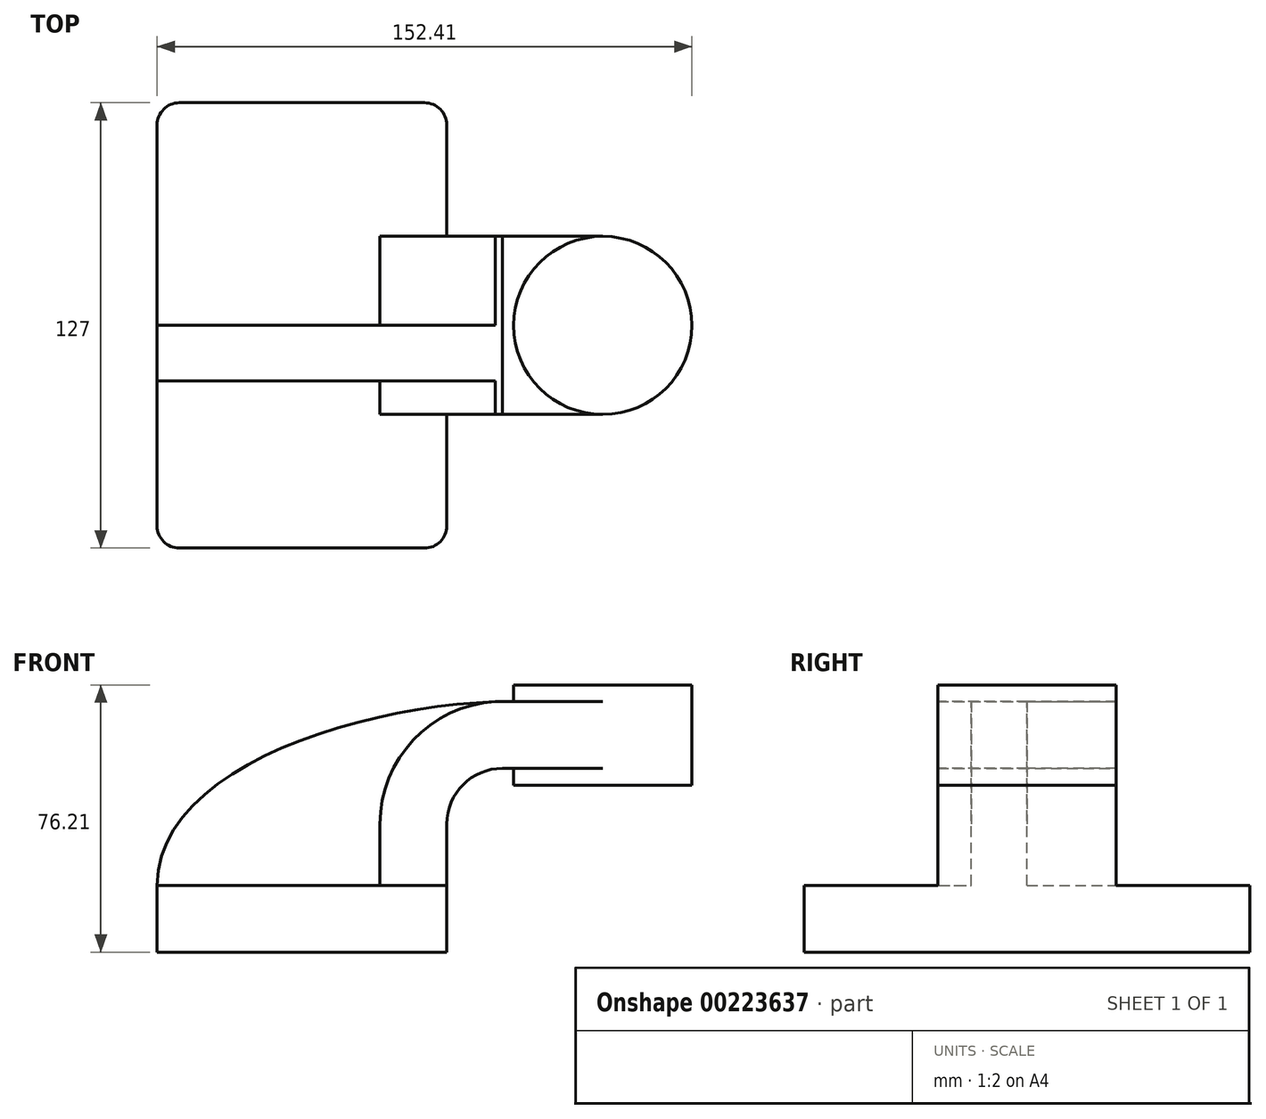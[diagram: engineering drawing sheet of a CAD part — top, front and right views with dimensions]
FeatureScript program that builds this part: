
annotation { "Feature Type Name" : "Feature", "Feature Type Description" : "" }
export const myFeature = defineFeature(function(context is Context, id is Id, definition is map)
    precondition{}
    {
        {
            var Q0;
            Q0=qCreatedBy(makeId("Front.planeOp"),FACE);
            var sketch = newSketch(context, id + "F0", { "sketchPlane" : qUnion([Q0])});
            skLineSegment(sketch, "E0.bottom", {"start": v(-41.27, -9.53) * mm, "end": v(41.28, -9.53) * mm});
            skLineSegment(sketch, "E0.top", {"start": v(-41.28, 9.53) * mm, "end": v(41.28, 9.53) * mm});
            skLineSegment(sketch, "E0.left", {"start": v(-41.28, -9.53) * mm, "end": v(-41.28, 9.53) * mm});
            skLineSegment(sketch, "E0.right", {"start": v(41.28, -9.53) * mm, "end": v(41.28, 9.53) * mm});
            skPoint(sketch, "E0.middle", {"position": v(0, 0) * mm});
            skLineSegment(sketch, "E1.bottom", {"start": v(60.33, 38.1) * mm, "end": v(111.12, 38.1) * mm});
            skLineSegment(sketch, "E1.top", {"start": v(60.33, 66.67) * mm, "end": v(111.12, 66.67) * mm});
            skLineSegment(sketch, "E1.left", {"start": v(60.33, 38.1) * mm, "end": v(60.33, 66.67) * mm});
            skLineSegment(sketch, "E1.right", {"start": v(111.12, 38.1) * mm, "end": v(111.12, 66.67) * mm});
            skPoint(sketch, "E1.middle", {"position": v(85.72, 52.39) * mm});
            skLineSegment(sketch, "E2", {"start": v(41.28, 9.52) * mm, "end": v(41.28, 27) * mm});
            skArc(sketch, "E3", {"start": v(41.27, 27) * mm, "mid": v(45.92, 38.23) * mm, "end": v(57.15, 42.88) * mm});
            skLineSegment(sketch, "E4", {"start": v(57.15, 42.88) * mm, "end": v(94.45, 42.88) * mm});
            skLineSegment(sketch, "E5.0", {"start": v(57.15, 61.93) * mm, "end": v(94.45, 61.93) * mm});
            skArc(sketch, "E5.1", {"start": v(22.22, 27) * mm, "mid": v(32.45, 51.7) * mm, "end": v(57.15, 61.93) * mm});
            skLineSegment(sketch, "E5.2", {"start": v(22.22, 9.52) * mm, "end": v(22.22, 27) * mm});
            skLineSegment(sketch, "E6", {"start": v(85.72, 38.1) * mm, "end": v(85.72, 66.67) * mm});
            skFitSpline(sketch, "E7", {"points": [v(-41.28, 9.53) * mm, v(57.15, 61.93) * mm], "startDerivative": vector(0.27, 100.74) * mm, "endDerivative": vector(122.34, 2.75) * mm});
            skSolve(sketch);
        }
        {
            var Q0;
            Q0=makeQuery(id+"F0.imprint","IMPRINT",FACE,{"disambiguationData":[TD([[makeQuery(id+"F0.imprint","IMPRINT",EDGE,{"derivedFrom":sQuery(id+"F0.wireOp",EDGE,"E0.bottom")}),1.0]])]});
            extrude(context, id + "F1", {"entities" : qUnion([Q0]), "endBound" : BoundingType.SYMMETRIC, "depth" : 127 * mm});
        }
        {
            var Q0;
            {var subQ1=sQuery(id+"F0.wireOp",EDGE,"E2");Q0=makeQuery(id+"F0.imprint","IMPRINT",FACE,{"disambiguationData":[TD([[makeQuery(id+"F0.imprint","IMPRINT",EDGE,{"derivedFrom":subQ1}),1.0]])]});}
            var Q1;
            {var subQ0=sQuery(id+"F0.wireOp",EDGE,"E4");var subQ1=sQuery(id+"F0.wireOp",EDGE,"E1.left");var subQ2=makeQuery(id+"F0.imprint","INTERSECT",VERTEX,{"derivedFrom":[subQ1,subQ0]});Q1=makeQuery(id+"F0.imprint","IMPRINT",FACE,{"disambiguationData":[TD([[makeQuery(id+"F0.imprint","IMPRINT",EDGE,{"disambiguationData":[TD([[subQ2,-1.0]])],"derivedFrom":subQ1}),-1.0]])]});}
            extrude(context, id + "F2", {"entities" : qUnion([Q0, Q1]), "operationType" : NewBodyOperationType.ADD, "endBound" : BoundingType.SYMMETRIC, "depth" : 50.8 * mm});
        }
        {
            var Q0;
            {var subQ3=sQuery(id+"F0.wireOp",EDGE,"E5.2");Q0=makeQuery(id+"F0.imprint","IMPRINT",FACE,{"disambiguationData":[TD([[makeQuery(id+"F0.imprint","IMPRINT",EDGE,{"derivedFrom":subQ3}),1.0]])]});}
            extrude(context, id + "F3", {"entities" : qUnion([Q0]), "operationType" : NewBodyOperationType.ADD, "depth" : 15.88 * mm});
        }
        {
            var Q0;
            {var subQ0=sQuery(id+"F0.wireOp",EDGE,"E1.right");Q0=makeQuery(id+"F0.imprint","IMPRINT",FACE,{"disambiguationData":[TD([[makeQuery(id+"F0.imprint","IMPRINT",EDGE,{"derivedFrom":subQ0}),1.0]])]});}
            var Q1;
            Q1=sQuery(id+"F0.wireOp",EDGE,"E6");
            revolve(context, id + "F4", {"operationType" : NewBodyOperationType.ADD, "entities" : qUnion([Q0]), "axis" : qUnion([Q1]), "revolveType" : RevolveType.FULL});
        }
        {
            var Q0;
            Q0=makeQuery(id+"F1.opExtrude","CAP_EDGE",EDGE,{"disambiguationData":[OSD([sQuery(id+"F0.wireOp",EDGE,"E0.left")])],"isStart":false});
            var Q1;
            Q1=makeQuery(id+"F1.opExtrude","CAP_EDGE",EDGE,{"disambiguationData":[OSD([sQuery(id+"F0.wireOp",EDGE,"E0.right")])],"isStart":false});
            var Q2;
            Q2=makeQuery(id+"F1.opExtrude","CAP_EDGE",EDGE,{"disambiguationData":[OSD([sQuery(id+"F0.wireOp",EDGE,"E0.left")])],"isStart":true});
            var Q3;
            Q3=makeQuery(id+"F1.opExtrude","CAP_EDGE",EDGE,{"disambiguationData":[OSD([sQuery(id+"F0.wireOp",EDGE,"E0.right")])],"isStart":true});
            fillet(context, id + "F5", {"entities" : qUnion([Q0, Q1, Q2, Q3]), "radius" : 6.35 * mm, "tangentPropagation" : true, "allowEdgeOverflow" : false});
        }
    });
